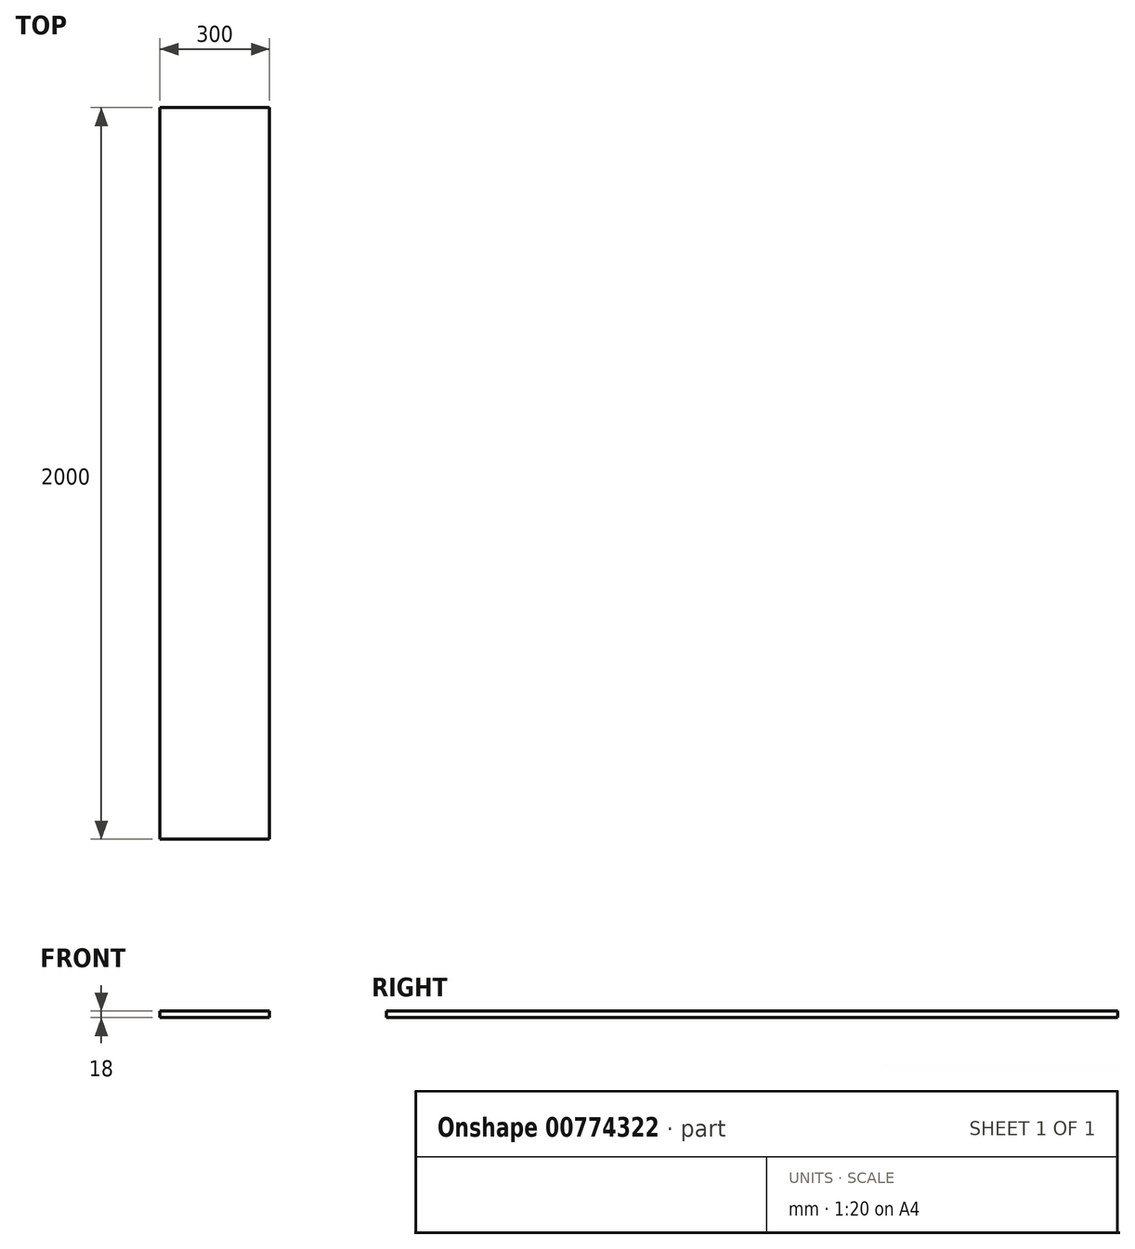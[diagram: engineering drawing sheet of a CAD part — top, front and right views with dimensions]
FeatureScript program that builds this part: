
annotation { "Feature Type Name" : "Feature", "Feature Type Description" : "" }
export const myFeature = defineFeature(function(context is Context, id is Id, definition is map)
    precondition{}
    {
        {
            var Q0;
            Q0=qCreatedBy(makeId("Top.planeOp"),FACE);
            var sketch = newSketch(context, id + "F0", { "sketchPlane" : qUnion([Q0])});
            skLineSegment(sketch, "E0.bottom", {"start": v(150, 1000) * mm, "end": v(-150, 1000) * mm});
            skLineSegment(sketch, "E0.top", {"start": v(150, -1000) * mm, "end": v(-150, -1000) * mm});
            skLineSegment(sketch, "E0.right", {"start": v(-150, 1000) * mm, "end": v(-150, -1000) * mm});
            skPoint(sketch, "E0.middle", {"position": v(0, 0) * mm});
            skLineSegment(sketch, "E1", {"start": v(150, 1000) * mm, "end": v(150, -1000) * mm});
            skSolve(sketch);
        }
        {
            var Q0;
            Q0=makeQuery(id+"F0.imprint","IMPRINT",FACE,{"disambiguationData":[TD([[makeQuery(id+"F0.imprint","IMPRINT",EDGE,{"derivedFrom":sQuery(id+"F0.wireOp",EDGE,"E0.bottom")}),1.0]])]});
            extrude(context, id + "F1", {"entities" : qUnion([Q0]), "depth" : 18 * mm, "offsetDistance" : 25 * mm});
        }
    });
